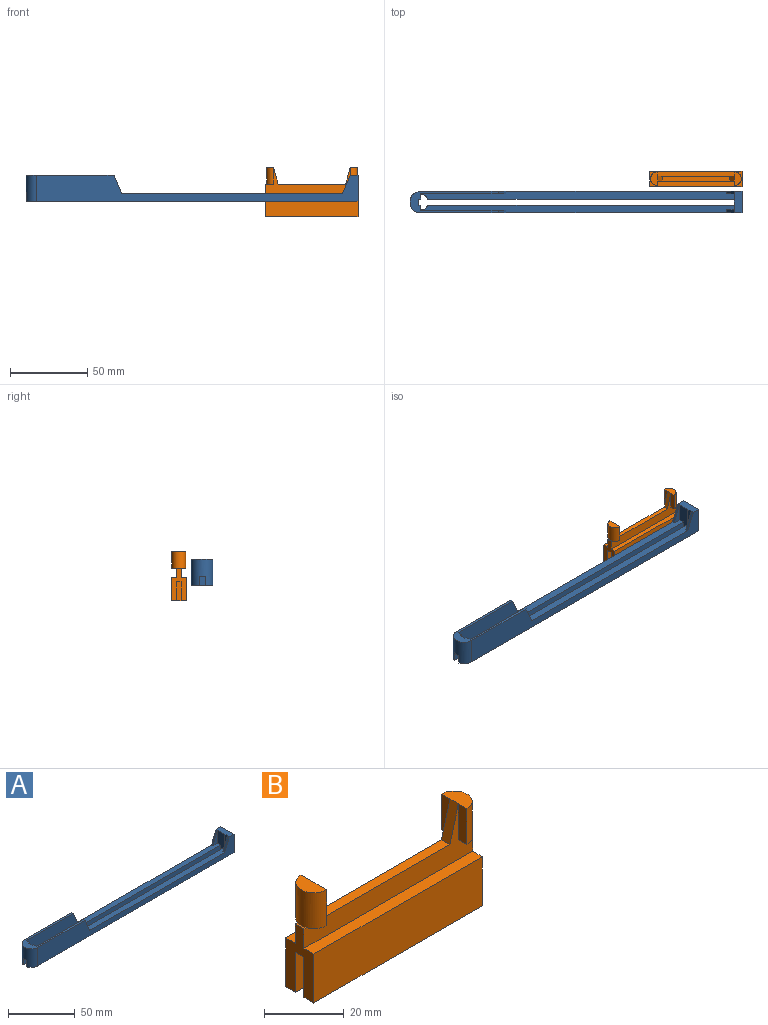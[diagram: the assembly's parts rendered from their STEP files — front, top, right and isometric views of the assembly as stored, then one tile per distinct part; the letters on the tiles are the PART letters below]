
ASSEMBLY  parts=2 mates=1
PART A: 29 faces, bbox 215x14x17 mm
  f0: plane 208x17mm, normal (0,-1,0), area 1760mm2, adj f3,f6,f8,f14,f15,f20,f25,f26
  f1: plane 12x5mm, normal (0,-1,0), area 30mm2, adj f9,f16,f27
  f2: plane 12x5.01mm, normal (0,1,0), area 30.1mm2, adj f6,f18,f20,f26
  f3: plane 57x14mm, normal (0,0,1), area 224.9mm2, adj f0,f4,f5,f7,f14,f17,f19,f21
  f4: plane 17x3.5mm, normal (1,0,0), area 57mm2, adj f3,f6,f12,f15,f19,f21
  f5: plane 17x3.5mm, normal (1,0,0), area 57mm2, adj f3,f11,f15,f16,f17,f22
  f6: plane 203.01x5mm, normal (0,0,1), area 909.2mm2, adj f0,f2,f4,f12,f13,f18,f19,f25
  f7: plane 208x17mm, normal (0,1,0), area 1760mm2, adj f3,f8,f14,f15,f16,f20,f27,f28
  f8: plane 17x14mm, normal (1,0,0), area 238mm2, adj f0,f7,f15,f20
  f9: plane 17x7.5mm, normal (-1,0,0), area 110mm2, adj f1,f10,f13,f15,f16,f18,f20
  f10: plane 198.42x5mm, normal (0,-1,0), area 992.1mm2, adj f9,f11,f15,f16
  f11: cylinder r=5mm len=5mm, axis (0,0,1), area 29mm2, adj f5,f10,f15,f16
  f12: cylinder r=5mm len=5mm, axis (0,0,1), area 29mm2, adj f4,f6,f13,f15
  f13: plane 198.42x5mm, normal (0,1,0), area 992.1mm2, adj f6,f9,f12,f15
  f14: cylinder r=7mm len=17mm, axis (0,0,1), area 349.5mm2, adj f0,f3,f7,f15,f21,f22,f23
  f15: plane 214.71x14mm, normal (0,0,-1), area 2129.5mm2, adj f0,f4,f5,f7,f8,f9,f10,f11
  f16: plane 203x5mm, normal (0,0,1), area 915.1mm2, adj f1,f5,f7,f9,f10,f11,f17,f27
  f17: plane 55x12mm, normal (0,-1,0), area 630mm2, adj f3,f5,f16,f28
  f18: plane 12x3.02mm, normal (-1,0,0), area 36.3mm2, adj f2,f6,f9,f20
  f19: plane 55x12mm, normal (0,1,0), area 630mm2, adj f3,f4,f6,f25
  f20: plane 14x5mm, normal (0,0,1), area 70mm2, adj f0,f2,f7,f8,f9,f18,f26,f27
  f21: plane 17x6.71mm, normal (0,1,0), area 69.1mm2, adj f3,f4,f14,f15,f23,f24
  f22: plane 17x6.71mm, normal (0,-1,0), area 69.1mm2, adj f3,f5,f14,f15,f23,f24
  f23: plane 4x3mm, normal (0,0,-1), area 11.6mm2, adj f14,f21,f22,f24
  f24: plane 11x4mm, normal (0.97,0,-0.24), area 45.4mm2, adj f3,f21,f22,f23
  f25: plane 12x5mm, normal (0.92,0,0.38), area 21.1mm2, adj f0,f3,f6,f19
  f26: plane 12x5mm, normal (-0.92,0,0.38), area 25.6mm2, adj f0,f2,f6,f20
  f27: plane 12x5mm, normal (-0.92,0,0.38), area 19.5mm2, adj f1,f7,f16,f20
  f28: plane 12x5mm, normal (0.92,0,0.38), area 19.5mm2, adj f3,f7,f16,f17
PART B: 30 faces, bbox 59.7x10x32 mm
  f0: plane 3x0.76mm, normal (0,0,1), area 1.8mm2, adj f6,f11,f12,f28
  f1: plane 3x0.76mm, normal (0,0,1), area 1.8mm2, adj f8,f11,f12,f22
  f2: plane 12.29x3mm, normal (-1,0,0), area 36.9mm2, adj f3,f15,f16,f17
  f3: plane 55x3mm, normal (0,0,-1), area 165mm2, adj f2,f6,f16,f17
  f4: plane 43.69x3mm, normal (0,0,1), area 131.1mm2, adj f11,f12,f13,f14
  f5: plane 59.69x3.5mm, normal (0,0,1), area 208.9mm2, adj f6,f8,f9,f12
  f6: plane 21x10mm, normal (-1,0,0), area 131.1mm2, adj f0,f3,f5,f7,f9,f10,f11,f12
  f7: plane 59.69x3.5mm, normal (0,0,1), area 208.9mm2, adj f6,f8,f10,f11
  f8: plane 21x10mm, normal (1,0,0), area 168mm2, adj f1,f5,f7,f9,f10,f11,f12,f15
  f9: plane 59.69x15mm, normal (0,1,0), area 895.4mm2, adj f5,f6,f8,f15
  f10: plane 59.69x15mm, normal (0,-1,0), area 895.4mm2, adj f6,f7,f8,f15
  f11: plane 59.69x17mm, normal (0,-1,0), area 391.2mm2, adj f0,f1,f4,f6,f7,f8,f13,f14
  f12: plane 59.69x17mm, normal (0,1,0), area 391.2mm2, adj f0,f1,f4,f5,f6,f8,f13,f14
  f13: plane 11x3mm, normal (-0.96,0,0.26), area 34.2mm2, adj f4,f11,f12,f23
  f14: plane 11x3mm, normal (0.96,0,0.26), area 34.2mm2, adj f4,f11,f12,f29
  f15: plane 59.69x10mm, normal (0,0,-1), area 431.9mm2, adj f2,f6,f8,f9,f10,f16,f17
  f16: plane 55x12.29mm, normal (0,1,0), area 676mm2, adj f2,f3,f6,f15
  f17: plane 55x12.29mm, normal (0,-1,0), area 676mm2, adj f2,f3,f6,f15
  f18: plane 11x3mm, normal (-1,0,0), area 33mm2, adj f11,f20,f22,f23
  f19: plane 11x3mm, normal (-1,0,0), area 33mm2, adj f12,f21,f22,f23
  f20: plane 4.24x3mm, normal (0,0,-1), area 9.3mm2, adj f11,f18,f22
  f21: plane 4.24x3mm, normal (0,0,-1), area 9.3mm2, adj f12,f19,f22
  f22: cylinder r=4.5mm len=11mm, axis (0,0,-1), area 155.5mm2, adj f1,f18,f19,f20,f21,f23
  f23: plane 9x4.5mm, normal (0,0,1), area 31.8mm2, adj f13,f18,f19,f22
  f24: plane 11x3mm, normal (1,0,0), area 33mm2, adj f11,f26,f28,f29
  f25: plane 11x3mm, normal (1,0,0), area 33mm2, adj f12,f27,f28,f29
  f26: plane 4.24x3mm, normal (0,0,-1), area 9.3mm2, adj f11,f24,f28
  f27: plane 4.24x3mm, normal (0,0,-1), area 9.3mm2, adj f12,f25,f28
  f28: cylinder r=4.5mm len=11mm, axis (0,0,-1), area 155.5mm2, adj f0,f24,f25,f26,f27,f29
  f29: plane 9x4.5mm, normal (0,0,1), area 31.8mm2, adj f14,f24,f25,f28
PLACE A t=(0,-13.16,0)mm
PLACE B at identity
MATE planar A.f8 <-> B.f8  axis (1,0,0) through (0,-20.16,8.5)mm
